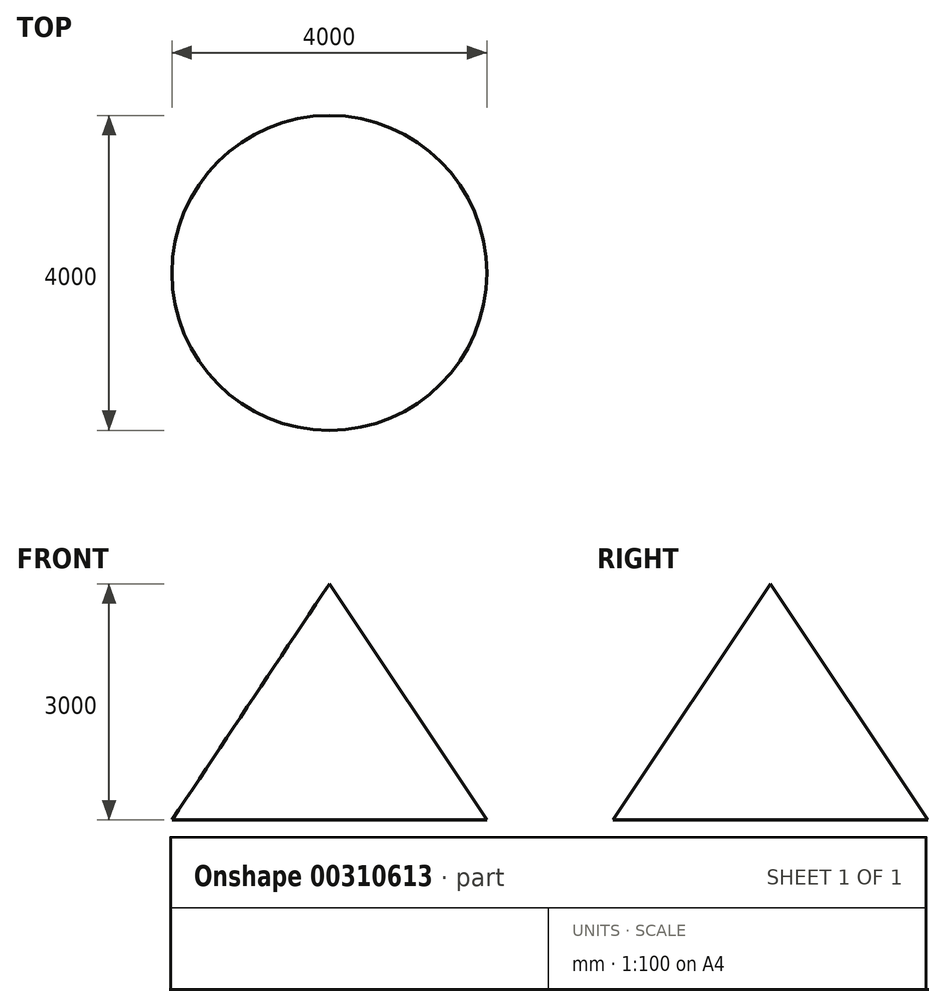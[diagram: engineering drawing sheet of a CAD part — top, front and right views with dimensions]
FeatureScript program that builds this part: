
annotation { "Feature Type Name" : "Feature", "Feature Type Description" : "" }
export const myFeature = defineFeature(function(context is Context, id is Id, definition is map)
    precondition{}
    {
        {
            var Q0;
            Q0=qCreatedBy(makeId("Front.planeOp"),FACE);
            var sketch = newSketch(context, id + "F0", { "sketchPlane" : qUnion([Q0])});
            skLineSegment(sketch, "E0", {"start": v(0, 0) * mm, "end": v(0, 3000) * mm});
            skLineSegment(sketch, "E1", {"start": v(0, 3000) * mm, "end": v(-2000, 0) * mm});
            skLineSegment(sketch, "E2", {"start": v(-2000, 0) * mm, "end": v(115.27, 0) * mm});
            skSolve(sketch);
        }
        {
            var Q0;
            {var subQ0=sQuery(id+"F0.wireOp",EDGE,"E0");Q0=makeQuery(id+"F0.imprint","IMPRINT",FACE,{"disambiguationData":[TD([[makeQuery(id+"F0.imprint","IMPRINT",EDGE,{"derivedFrom":subQ0}),1.0]])]});}
            var Q1;
            Q1=sQuery(id+"F0.wireOp",EDGE,"9WkHhQZQ-dKgy-4zfv-GDi7-WJvomRhu1KfC");
            var Q2;
            Q2=sQuery(id+"F0.wireOp",EDGE,"E0");
            revolve(context, id + "F1", {"entities" : qUnion([Q0]), "surfaceEntities" : qUnion([Q1]), "axis" : qUnion([Q2]), "revolveType" : RevolveType.FULL});
        }
    });
